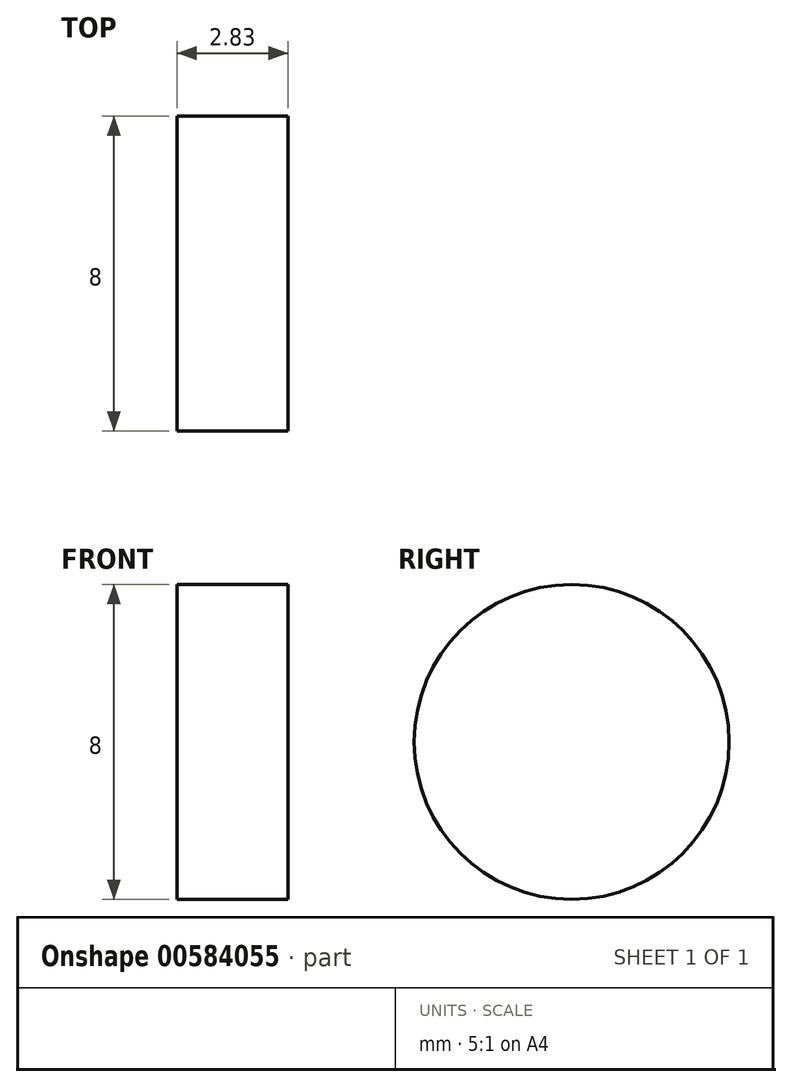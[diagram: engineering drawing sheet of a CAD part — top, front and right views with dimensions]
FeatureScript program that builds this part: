
annotation { "Feature Type Name" : "Feature", "Feature Type Description" : "" }
export const myFeature = defineFeature(function(context is Context, id is Id, definition is map)
    precondition{}
    {
        {
            var Q0;
            Q0=qCreatedBy(makeId("Right.planeOp"),FACE);
            var sketch = newSketch(context, id + "F0", { "sketchPlane" : qUnion([Q0])});
            skCircle(sketch, "E0", {"center": v(0, 0) * mm, "radius": 4 * mm});
            skSolve(sketch);
        }
        {
            var Q0;
            Q0 = qSketchRegion(id + "F0", true);
            extrude(context, id + "F1", {"entities" : qUnion([Q0]), "depth" : 2.83 * mm, "offsetDistance" : 25 * mm});
        }
    });
